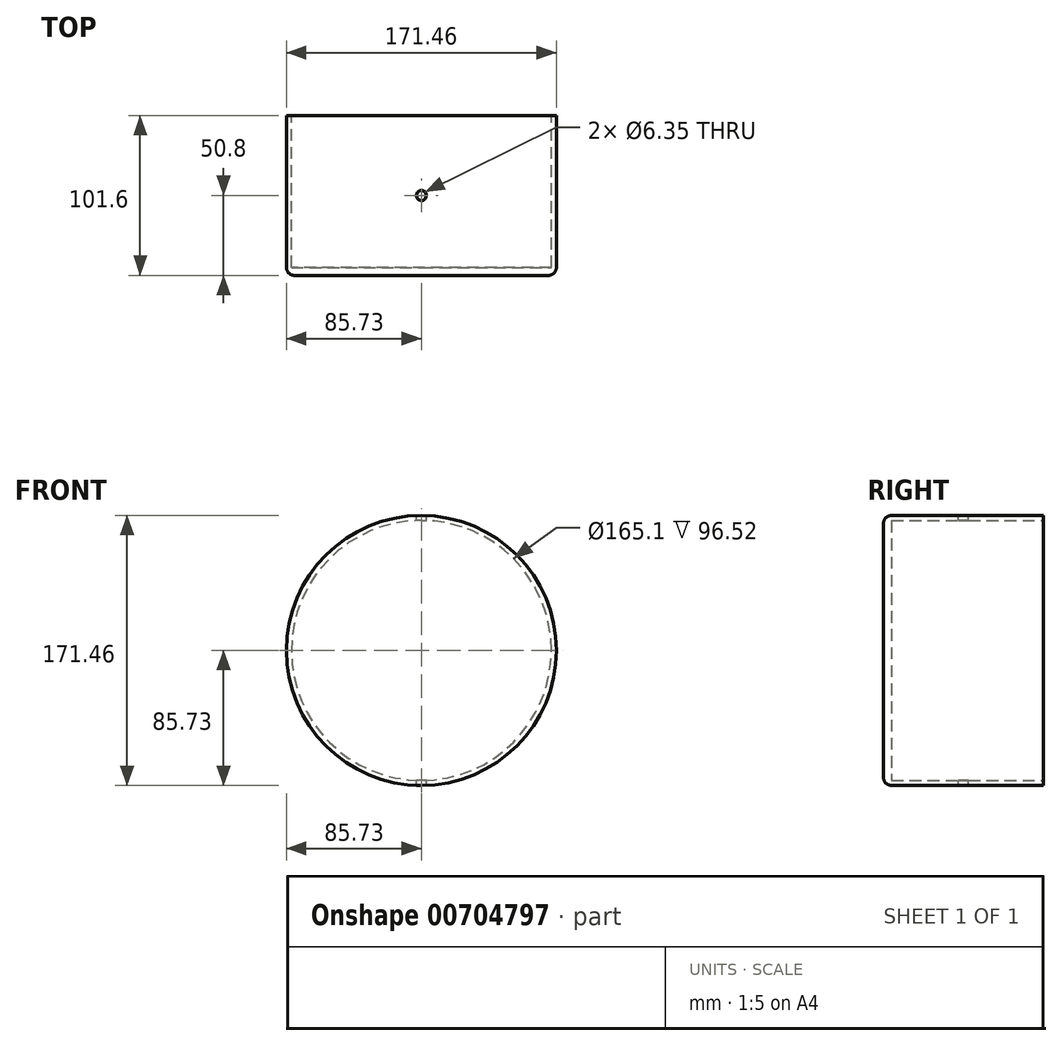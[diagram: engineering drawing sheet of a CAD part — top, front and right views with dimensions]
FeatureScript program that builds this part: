
annotation { "Feature Type Name" : "Feature", "Feature Type Description" : "" }
export const myFeature = defineFeature(function(context is Context, id is Id, definition is map)
    precondition{}
    {
        {
            var Q0;
            Q0=qCreatedBy(makeId("Front.planeOp"),FACE);
            var sketch = newSketch(context, id + "F0", { "sketchPlane" : qUnion([Q0])});
            skCircle(sketch, "E0", {"center": v(0, 0) * mm, "radius": 85.73 * mm});
            skSolve(sketch);
        }
        {
            var Q0;
            Q0 = qSketchRegion(id + "F0", true);
            extrude(context, id + "F1", {"entities" : qUnion([Q0]), "oppositeDirection" : true, "depth" : 101.6 * mm, "offsetDistance" : 25.4 * mm});
        }
        {
            var Q0;
            Q0=makeQuery(id+"F1.opExtrude","CAP_FACE",FACE,{"disambiguationData":[OSD([sQuery(id+"F0.wireOp",EDGE,"E0")])],"isStart":false});
            var sketch = newSketch(context, id + "F2", { "sketchPlane" : qUnion([Q0])});
            skCircle(sketch, "E1", {"center": v(0, 0) * mm, "radius": 82.55 * mm});
            skSolve(sketch);
        }
        {
            var Q0;
            Q0 = qSketchRegion(id + "F2", true);
            extrude(context, id + "F3", {"entities" : qUnion([Q0]), "operationType" : NewBodyOperationType.REMOVE, "oppositeDirection" : true, "depth" : 96.52 * mm, "offsetDistance" : 25.4 * mm});
        }
        {
            var Q0;
            Q0=makeQuery(id+"F1.opExtrude","CAP_EDGE",EDGE,{"disambiguationData":[OSD([sQuery(id+"F0.wireOp",EDGE,"E0")])],"isStart":true});
            fillet(context, id + "F4", {"entities" : qUnion([Q0]), "radius" : 5.08 * mm, "tangentPropagation" : true, "allowEdgeOverflow" : false});
        }
        {
            var Q0;
            Q0=qCreatedBy(makeId("Top.planeOp"),FACE);
            var sketch = newSketch(context, id + "F5", { "sketchPlane" : qUnion([Q0])});
            skCircle(sketch, "E2", {"center": v(0, 50.8) * mm, "radius": 3.17 * mm});
            skSolve(sketch);
        }
        {
            var Q0;
            Q0 = qSketchRegion(id + "F5", true);
            extrude(context, id + "F6", {"entities" : qUnion([Q0]), "operationType" : NewBodyOperationType.REMOVE, "endBound" : BoundingType.SYMMETRIC, "oppositeDirection" : true, "depth" : 508 * mm, "offsetDistance" : 25.4 * mm});
        }
    });
